# Revit family: 3f_filippi_-_zero_3f_3f_filippi_-_1861_-_03f_44w-940_l1506
name_source: partatom
category: Lighting Fixtures
units: mm (PartAtom-declared; Revit-internal decimal feet)

## family parameters
Cut with Voids When Loaded = No
Host = Face
Light Source = No
Part Type = Normal
Room Calculation Point = No
Round Connector Dimension = Use Diameter
Shared = No

## types (1)
- 3F Filippi - Zero 3F (1 x LED, 5190 lm, 50 W, 4000 K)
    Apparent Load = 50 VA
    Approval mark = CE
    CIE Flux Codes = 55 84 94 83 100
    Color Rendering = 90
    Color Temperature = 4000 K
    Control Gear = Electronic ballast
    Default Elevation = 1800 mm
    Description = ILLUMINOTECHNICAL
Luminous efficiency 100% (DLOR 83%, ULOR 17%).
Initial luminous flux of the luminaire 5190 lm.
Controlled symmetric distribution.
Installation Interdistance Transv.D = 1.32 x hu - Long.D = 1.30 x hu.
Average luminance <3000 cd/m² for radial angles >65°.
Tabular UGR (CIE 117 - 4H-8H; S=0.25H; 70/50/20): RUG 19.1 - 17.9.
Beam angle: 99° - 100°.
Luminous efficacy 104 lm/W.
Lifetime (L93/B10): 30000 h. (tq+25°C)
Lifetime (L90/B10): 50000 h. (tq+25°C)
Lifetime (L85/B10): 80000 h. (tq+25°C)
Lifetime (L80/B10): 100000 h. (tq+25°C)
Sudden decreased luminous flux after 50000 hours: 0% (C0).
Photobiological safety in compliance with IEC/TR 62778: RG0 risk exempt, (IEC 62471).
In compliance with IEC/EN 62722-2-1 - IEC/EN 62717 standards.

SOURCE
Linear LED module 44W/940.
Energy efficiency class (UE 2019/2020 - UE 2019/2015): E.
CIE 13.3 Colour rendering index: CRI >90 (R9 >50%).
IES TM-30 Fidelity Index: Rf = 92 Rg = 101.
CCT nominal colour temperature 4000 K.
Colour initial tolerance (MacAdam): SDCM 3.

MECHANICAL
Housing in hot-galvanised steel, painted in white polyester.
Diffuser with differentiated geometry, made of transparent methacrylate (PMMA) with microprismatic finish, anti-glare on the flat part and opal on the side.
Anti-glare opal methacrylate (PMMA) filter for brightness uniformity.
Lighting end caps in methacrylate (PMMA) opal.
Luminaire with limited surface temperature. - D - (EN 60598-2-24)
Dimensions: 1506x119 mm, height 64 mm. Weight 2.715 kg.
IP40 protection degree.
Mechanical strength to impacts IK06 (1 joule).
Glow-wire test resistance 650°C.

ELECTRICAL
Halogen Free electronic wiring 230V-50/60Hz, power factor 0.95, THD <25%, constant output current, SELV, class I, 1 driver.
Power of the luminaire 50 W.
ENEC - CE.
SAFE FLICKER: PstLM=<1 and SVM=<0.4 (IEC TR 61547-1 and IEC TR 63158), to ensure a more comfortable and safe light.
Luminaire compliant with EN 60598-2-22 for power supply from a centralised emergency system CPSS (Central Power Supply System), not incorporated in the luminaire - high risk areas excluded. The default power and flux are 100% in AC and 100% in DC.
Ambient temperature from +5°C to +25°C.
Temperature class T6 max 85°C.
Relative humidity UR: <85%.

INSTALLATION
Ceiling / Suspended / Wall.
Thanks to the full compatibility for dimensions and fixing distances, this product becomes the perfect solution for updating existing installations.
All accessories dedicated to this product are available on the Catalog and on our website www.3F-Filippi.com.

APPLICATIONS
Suitable product for food production plants (HACCP), IFS (Food Version 6), BRC (GSFS Food Version 7).
Environments: with VDTs, meeting rooms, offices.
Environments: recreational, transit areas, corridors, schools, stairwells.
Environments where soft diffuse light is required for optimal visual comfort.

WARNING
Luminaire designed for disposal/recycling at end-of-life.
Replaceable (LED only) light source by a professional. Replaceable control gear by a professional.
    Height = 64 mm
    Lamp = 1 x LED
    Lamp Light Flux = 5190 lm
    Lamp Power = 50 W
    Lamp count = 1
    Length = 1506 mm
    Lifetime = 50000 h
    Luminous efficacy = 104 lm/W
    Manufacturer = 3F Filippi
    ModVariant = No
    Model = 3F Filippi - 1861 - 03F 44W-940 L1506
    Mounting Place = Ceiling
    Mounting Type = Surface mounted
    Number of Poles = 1
    OnlyDefault = Yes
    Power Factor = 1
    Product Name = 3F Filippi - Zero 3F
    Product group = ceiling mounted luminaire
    ProductGroupID = 3
    Protection Class = Protection class I
    Protection Degree = IP 40
    RLX_Detail_Level = 1
    RLX_Emergency_Light_Flux = 0 lm
    RLX_Emergency_Type = 0
    RLX_Emergency_Type_DB = No
    RlxData = <blob elided: 147625 chars, md5=2bd44e34>
    Socket = socket
    Standby Power = 0 W
    System Light Flux = 5190 lm
    System Power = 50 W
    Type Comments = Product without accessories
    Type Image = 3ffilippi_zero_3f.jpg
    URL = http://relux.com
    VarID = ---
    Voltage = 0 V
    Weight = 0.00 kg
    Width = 119 mm

## geometry (parser evidence)
native form markers: Sweep x13
no freeform markers — native parametric forms only
